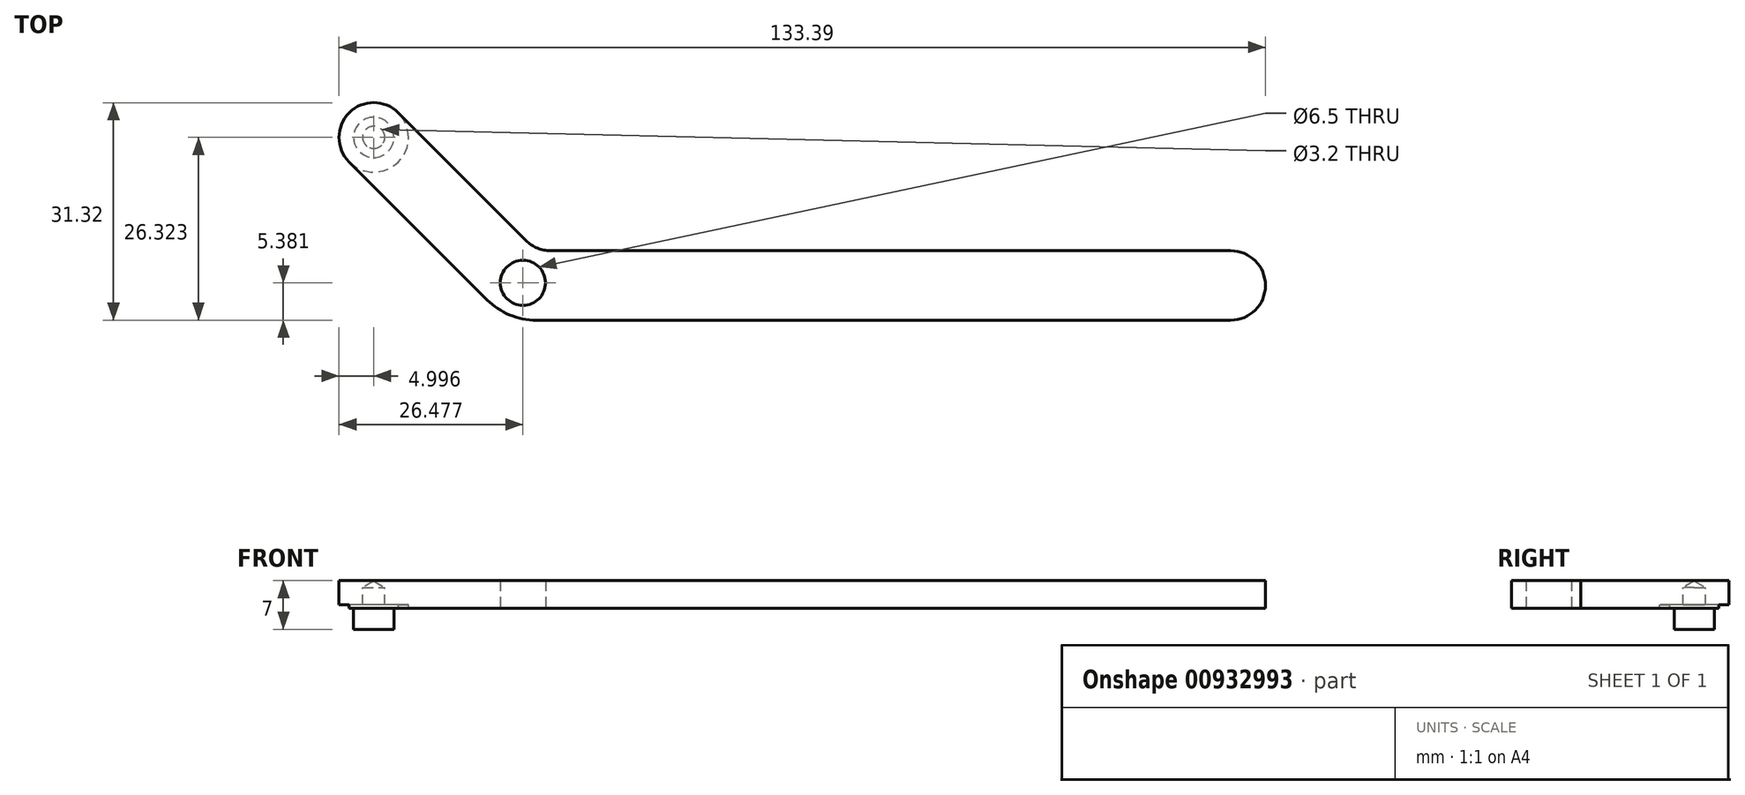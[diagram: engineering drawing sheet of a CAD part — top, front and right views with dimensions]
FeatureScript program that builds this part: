
annotation { "Feature Type Name" : "Feature", "Feature Type Description" : "" }
export const myFeature = defineFeature(function(context is Context, id is Id, definition is map)
    precondition{}
    {
        {
            var Q0;
            Q0=qCreatedBy(makeId("Top.planeOp"),FACE);
            var sketch = newSketch(context, id + "F0", { "sketchPlane" : qUnion([Q0])});
            skLineSegment(sketch, "E0.bottom", {"start": v(0, 5) * mm, "end": v(100, 5) * mm});
            skLineSegment(sketch, "E0.top", {"start": v(0, -5) * mm, "end": v(100, -5) * mm});
            skLineSegment(sketch, "E0.right", {"start": v(100, 5) * mm, "end": v(100, -5) * mm});
            skLineSegment(sketch, "E1", {"start": v(0, 5) * mm, "end": v(-19.86, 24.86) * mm});
            skLineSegment(sketch, "E2", {"start": v(-19.86, 24.86) * mm, "end": v(-26.93, 17.79) * mm});
            skLineSegment(sketch, "E3", {"start": v(-26.93, 17.79) * mm, "end": v(-7.07, -2.07) * mm});
            skLineSegment(sketch, "E4", {"start": v(-7.07, -2.07) * mm, "end": v(0, 5) * mm});
            skArc(sketch, "E5", {"start": v(-19.86, 24.86) * mm, "mid": v(-26.93, 24.86) * mm, "end": v(-26.93, 17.79) * mm});
            skArc(sketch, "E6", {"start": v(100, -5) * mm, "mid": v(105, 0) * mm, "end": v(100, 5) * mm});
            skCircle(sketch, "E7", {"center": v(-1.91, 0.38) * mm, "radius": 3.25 * mm});
            skArc(sketch, "E8", {"start": v(-7.07, -2.07) * mm, "mid": v(-3.83, -4.24) * mm, "end": v(0, -5) * mm});
            skLineSegment(sketch, "E9", {"start": v(0, 5) * mm, "end": v(-3.83, -4.24) * mm, "construction": true});
            skLineSegment(sketch, "E10", {"start": v(0, 5) * mm, "end": v(0, -5) * mm});
            skSolve(sketch);
        }
        {
            var Q0;
            Q0=makeQuery(id+"F0.imprint","IMPRINT",FACE,{"disambiguationData":[TD([[makeQuery(id+"F0.imprint","IMPRINT",EDGE,{"derivedFrom":sQuery(id+"F0.wireOp",EDGE,"E1")}),1.0]])]});
            var Q1;
            Q1=makeQuery(id+"F0.imprint","IMPRINT",FACE,{"disambiguationData":[TD([[makeQuery(id+"F0.imprint","IMPRINT",EDGE,{"derivedFrom":sQuery(id+"F0.wireOp",EDGE,"E2")}),-1.0]])]});
            var Q2;
            Q2=makeQuery(id+"F0.imprint","IMPRINT",FACE,{"disambiguationData":[TD([[makeQuery(id+"F0.imprint","IMPRINT",EDGE,{"derivedFrom":sQuery(id+"F0.wireOp",EDGE,"XlTk1D1j-VJ7y-ry1h-NVlK-bYyykLbfSXm6.left")}),-1.0]])]});
            var Q3;
            Q3=makeQuery(id+"F0.imprint","IMPRINT",FACE,{"disambiguationData":[TD([[makeQuery(id+"F0.imprint","IMPRINT",EDGE,{"derivedFrom":sQuery(id+"F0.wireOp",EDGE,"E0.bottom")}),-1.0]])]});
            var Q4;
            Q4=makeQuery(id+"F0.imprint","IMPRINT",FACE,{"disambiguationData":[TD([[makeQuery(id+"F0.imprint","IMPRINT",EDGE,{"derivedFrom":sQuery(id+"F0.wireOp",EDGE,"E0.right")}),1.0]])]});
            var Q5;
            Q5=makeQuery(id+"F0.imprint","IMPRINT",FACE,{"disambiguationData":[TD([[makeQuery(id+"F0.imprint","IMPRINT",EDGE,{"derivedFrom":sQuery(id+"F0.wireOp",EDGE,"E4")}),-1.0]])]});
            var Q6;
            {var subQ0=sQuery(id+"F0.wireOp",EDGE,"E8");Q6=makeQuery(id+"F0.imprint","IMPRINT",FACE,{"disambiguationData":[TD([[makeQuery(id+"F0.imprint","IMPRINT",EDGE,{"derivedFrom":subQ0}),1.0]])]});}
            extrude(context, id + "F1", {"entities" : qUnion([Q0, Q1, Q2, Q3, Q4, Q5, Q6]), "depth" : 3.5 * mm, "offsetDistance" : 25 * mm});
        }
        {
            var Q0;
            Q0=makeQuery(id+"F1.opExtrude","CAP_FACE",FACE,{"disambiguationData":[OSD([sQuery(id+"F0.wireOp",EDGE,"E0.bottom"),sQuery(id+"F0.wireOp",EDGE,"E0.top"),sQuery(id+"F0.wireOp",EDGE,"E1"),sQuery(id+"F0.wireOp",EDGE,"E3"),sQuery(id+"F0.wireOp",EDGE,"E5"),sQuery(id+"F0.wireOp",EDGE,"E6"),sQuery(id+"F0.wireOp",EDGE,"E7"),sQuery(id+"F0.wireOp",EDGE,"E8")])],"isStart":true});
            var sketch = newSketch(context, id + "F2", { "sketchPlane" : qUnion([Q0])});
            skCircle(sketch, "E11", {"center": v(-23.4, -21.32) * mm, "radius": 5 * mm});
            skSolve(sketch);
        }
        {
            var Q0;
            {var subQ0=sQuery(id+"F2.wireOp",EDGE,"E11");Q0=makeQuery(id+"F2.imprint","IMPRINT",FACE,{"disambiguationData":[TD([[makeQuery(id+"F2.imprint","IMPRINT",EDGE,{"disambiguationData":[OD(0.0)],"derivedFrom":subQ0}),-1.0]])]});}
            extrude(context, id + "F3", {"entities" : qUnion([Q0]), "operationType" : NewBodyOperationType.ADD, "depth" : 0.5 * mm, "offsetDistance" : 25 * mm});
        }
        {
            var Q0;
            Q0=makeQuery(id+"F3.opExtrude","CAP_FACE",FACE,{"disambiguationData":[OSD([sQuery(id+"F2.wireOp",EDGE,"E11")])],"isStart":false});
            var sketch = newSketch(context, id + "F4", { "sketchPlane" : qUnion([Q0])});
            skPoint(sketch, "E12", {"position": v(-23.4, -21.32) * mm});
            skSolve(sketch);
        }
        {
            var Q0;
            Q0=sQuery(id+"F4.wireOp",VERTEX,"E12");
            var Q1;
            Q1=makeQuery(id+"F1.opExtrude","SWEPT_BODY",BODY,{"disambiguationData":[OSD([sQuery(id+"F0.wireOp",EDGE,"E0.bottom"),sQuery(id+"F0.wireOp",EDGE,"E0.top"),sQuery(id+"F0.wireOp",EDGE,"E1"),sQuery(id+"F0.wireOp",EDGE,"E3"),sQuery(id+"F0.wireOp",EDGE,"E5"),sQuery(id+"F0.wireOp",EDGE,"E6"),sQuery(id+"F0.wireOp",EDGE,"E7"),sQuery(id+"F0.wireOp",EDGE,"E8")])]});
            hole(context, id + "F5", {"style" : HoleStyle.SIMPLE, "endStyle" : HoleEndStyle.BLIND, "holeDiameter" : 3.2 * mm, "majorDiameter" : 5 * mm, "holeDepth" : 2.5 * mm, "isTappedThrough" : true, "tappedDepth" : 12 * mm, "tapClearance" : 3, "locations" : qUnion([Q0]), "scope" : qUnion([Q1]), "startStyle" : HoleStartStyle.PART});
        }
        {
            var Q0;
            Q0=makeQuery(id+"F3.opExtrude","CAP_FACE",FACE,{"disambiguationData":[OSD([sQuery(id+"F2.wireOp",EDGE,"E11")])],"isStart":false});
            var sketch = newSketch(context, id + "F6", { "sketchPlane" : qUnion([Q0])});
            skCircle(sketch, "E13", {"center": v(-23.4, -21.32) * mm, "radius": 2.9 * mm});
            skSolve(sketch);
        }
        {
            var Q0;
            Q0=makeQuery(id+"F6.imprint","IMPRINT",FACE,{"disambiguationData":[TD([[makeQuery(id+"F6.imprint","IMPRINT",EDGE,{"derivedFrom":sQuery(id+"F6.wireOp",EDGE,"E13")}),1.0]])]});
            extrude(context, id + "F7", {"entities" : qUnion([Q0]), "operationType" : NewBodyOperationType.ADD, "depth" : 3 * mm, "offsetDistance" : 25 * mm});
        }
        {
            var Q0;
            Q0=makeQuery(id+"F1.opExtrude","SWEPT_EDGE",EDGE,{"disambiguationData":[OSD([sQuery(id+"F0.wireOp",EDGE,"E0.bottom"),sQuery(id+"F0.wireOp",EDGE,"E1"),sQuery(id+"F0.wireOp",EDGE,"E4"),sQuery(id+"F0.wireOp",EDGE,"E10")])]});
            fillet(context, id + "F8", {"entities" : qUnion([Q0]), "radius" : 5 * mm, "tangentPropagation" : true, "allowEdgeOverflow" : false});
        }
    });
